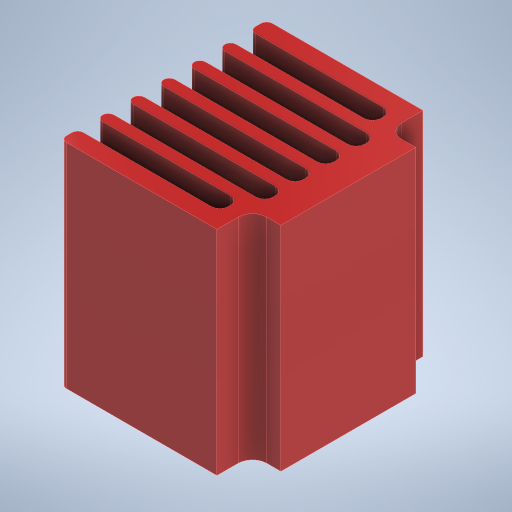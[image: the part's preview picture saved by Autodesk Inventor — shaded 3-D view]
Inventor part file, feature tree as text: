
AUTODESK INVENTOR PART (.ipt)
format: ipt  version: 2023.1 (Build 271208000, 208)  size: 302,080 bytes
history: native  units: mm
features: extrude x1, fillet x1, sketch x1
ambient origin geometry x8: Origin, YZ Plane, XZ Plane, XY Plane, X Axis, Y Axis, Z Axis, Center Point
bodies: Volumenkörper1 (feature_tree)
feature tree (3):
  extrude  "Extrusion1"  Depth=14.5mm
  fillet  "Rundung1"  Radius=2.0mm
  sketch  "Skizze1"  dims[d0=13.0mm d1=14.5mm d2=2.0mm d3=2.5mm d4=1.0mm d5=10.0mm d6=1.35mm d7=11.0mm d8=1.35mm d9=1.2mm d10=0.8mm d11=11.0mm d12=1.35mm d13=0.8mm d14=0.8mm d15=0.6mm d16=15.0mm d17=0.0mm d18=0.4mm]
